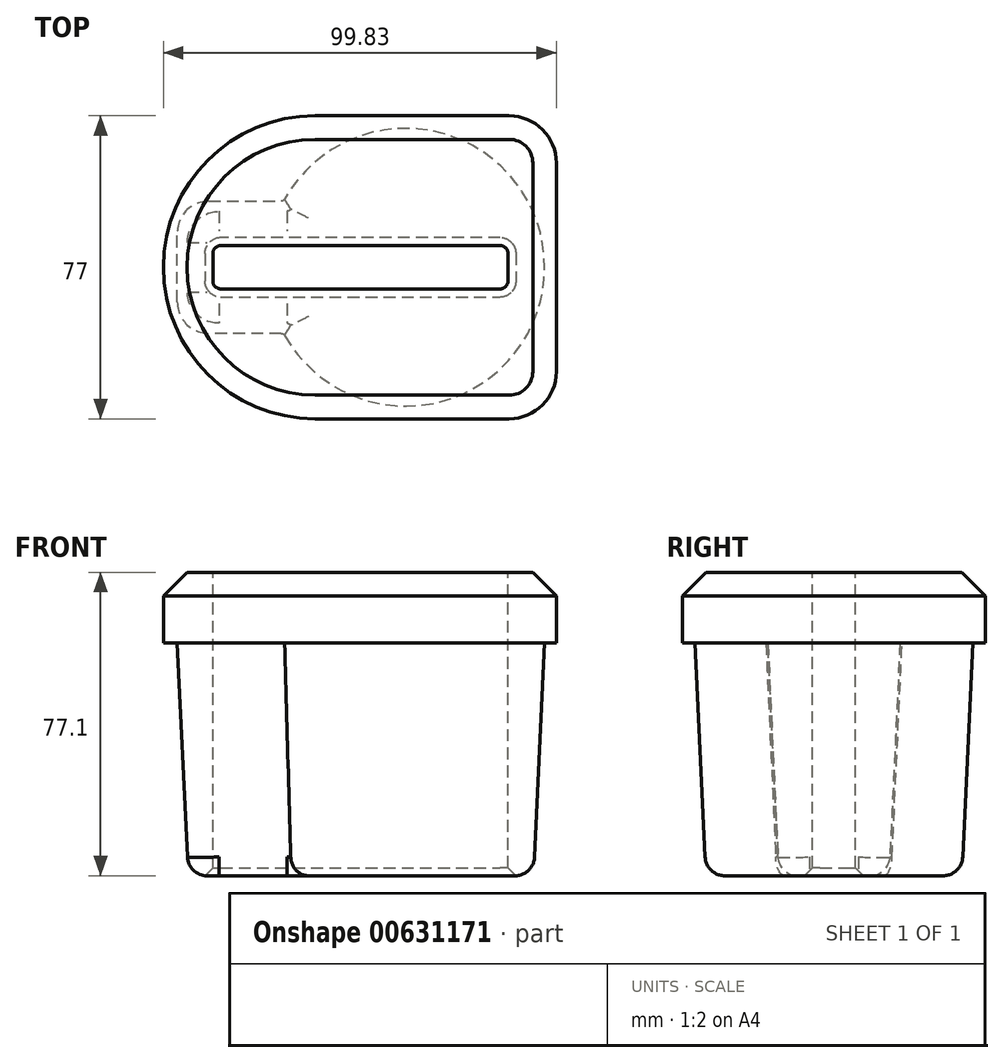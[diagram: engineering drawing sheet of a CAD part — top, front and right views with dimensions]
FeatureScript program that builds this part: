
annotation { "Feature Type Name" : "Feature", "Feature Type Description" : "" }
export const myFeature = defineFeature(function(context is Context, id is Id, definition is map)
    precondition{}
    {
        {
            var Q0;
            Q0=qCreatedBy(makeId("Top.planeOp"),FACE);
            var sketch = newSketch(context, id + "F0", { "sketchPlane" : qUnion([Q0])});
            skCircle(sketch, "E0", {"center": v(0, 0) * mm, "radius": 32.5 * mm});
            skLineSegment(sketch, "E1.bottom", {"start": v(-55.25, -14) * mm, "end": v(0, -14) * mm});
            skLineSegment(sketch, "E1.top", {"start": v(-55.25, 14) * mm, "end": v(0, 14) * mm});
            skLineSegment(sketch, "E1.left", {"start": v(-55.25, -14) * mm, "end": v(-55.25, 14) * mm});
            skLineSegment(sketch, "E1.right", {"start": v(0, -14) * mm, "end": v(0, 14) * mm});
            skSolve(sketch);
        }
        {
            var Q0;
            {var subQ5=sQuery(id+"F0.wireOp",EDGE,"E1.right");Q0=makeQuery(id+"F0.imprint","IMPRINT",FACE,{"disambiguationData":[TD([[makeQuery(id+"F0.imprint","IMPRINT",EDGE,{"derivedFrom":subQ5}),-1.0]])]});}
            var Q1;
            {var subQ5=sQuery(id+"F0.wireOp",EDGE,"E1.right");Q1=makeQuery(id+"F0.imprint","IMPRINT",FACE,{"disambiguationData":[TD([[makeQuery(id+"F0.imprint","IMPRINT",EDGE,{"derivedFrom":subQ5}),1.0]])]});}
            extrude(context, id + "F1", {"entities" : qUnion([Q0, Q1]), "depth" : 59.1 * mm, "offsetDistance" : 25 * mm, "hasDraft" : true, "draftAngle" : 2.7 * degree});
        }
        {
            var Q0;
            {var subQ5=sQuery(id+"F0.wireOp",EDGE,"E1.left");Q0=makeQuery(id+"F0.imprint","IMPRINT",FACE,{"disambiguationData":[TD([[makeQuery(id+"F0.imprint","IMPRINT",EDGE,{"derivedFrom":subQ5}),-1.0]])]});}
            extrude(context, id + "F2", {"entities" : qUnion([Q0]), "operationType" : NewBodyOperationType.ADD, "depth" : 59.1 * mm, "offsetDistance" : 25 * mm, "hasDraft" : true, "draftAngle" : 2.7 * degree});
        }
        {
            var Q0;
            {var subQ0=sQuery(id+"F0.wireOp",EDGE,"E0");Q0=makeQuery(id+"F2.boolean.opBoolean","MERGE",FACE,{"derivedFrom":[makeQuery(id+"F1.opExtrude","CAP_FACE",FACE,{"disambiguationData":[OSD([subQ0])],"isStart":false}),makeQuery(id+"F2.opExtrude","CAP_FACE",FACE,{"disambiguationData":[OSD([subQ0,sQuery(id+"F0.wireOp",EDGE,"E1.bottom"),sQuery(id+"F0.wireOp",EDGE,"E1.top"),sQuery(id+"F0.wireOp",EDGE,"E1.left")])],"isStart":false})]});}
            var sketch = newSketch(context, id + "F3", { "sketchPlane" : qUnion([Q0])});
            skArc(sketch, "E2", {"start": v(-23.04, 38.5) * mm, "mid": v(-61.54, 0) * mm, "end": v(-23.04, -38.5) * mm});
            skPoint(sketch, "E2.centerSnap0", {"position": v(-58.04, 0) * mm});
            skLineSegment(sketch, "E3.bottom", {"start": v(-23.04, -38.5) * mm, "end": v(26.29, -38.5) * mm});
            skLineSegment(sketch, "E3.top", {"start": v(-23.04, 38.5) * mm, "end": v(26.29, 38.5) * mm});
            skLineSegment(sketch, "E3.right", {"start": v(38.29, -26.5) * mm, "end": v(38.29, 26.5) * mm});
            skPoint(sketch, "E4.visualSharp", {"position": v(38.29, 38.5) * mm});
            skArc(sketch, "E4.filletArc", {"start": v(38.29, 26.5) * mm, "mid": v(34.77, 34.99) * mm, "end": v(26.29, 38.5) * mm});
            skPoint(sketch, "E5.visualSharp", {"position": v(38.29, -38.5) * mm});
            skArc(sketch, "E5.filletArc", {"start": v(26.29, -38.5) * mm, "mid": v(34.77, -34.99) * mm, "end": v(38.29, -26.5) * mm});
            skSolve(sketch);
        }
        {
            var Q0;
            Q0=makeQuery(id+"F2.opExtrude","SWEPT_EDGE",EDGE,{"disambiguationData":[OSD([sQuery(id+"F0.wireOp",EDGE,"E1.top"),sQuery(id+"F0.wireOp",EDGE,"E1.left")])]});
            var Q1;
            Q1=makeQuery(id+"F2.opExtrude","SWEPT_EDGE",EDGE,{"disambiguationData":[OSD([sQuery(id+"F0.wireOp",EDGE,"E1.bottom"),sQuery(id+"F0.wireOp",EDGE,"E1.left")])]});
            fillet(context, id + "F4", {"entities" : qUnion([Q0, Q1]), "radius" : 8 * mm, "tangentPropagation" : true, "allowEdgeOverflow" : false});
        }
        {
            var Q0;
            Q0=makeQuery(id+"F2.boolean.opBoolean","INTERSECT",EDGE,{"derivedFrom":[makeQuery(id+"F1.opExtrude","SWEPT_FACE",FACE,{"disambiguationData":[OSD([sQuery(id+"F0.wireOp",EDGE,"E0")])]}),makeQuery(id+"F2.opExtrude","SWEPT_FACE",FACE,{"disambiguationData":[OSD([sQuery(id+"F0.wireOp",EDGE,"E1.bottom")])]})]});
            var Q1;
            Q1=makeQuery(id+"F2.boolean.opBoolean","INTERSECT",EDGE,{"derivedFrom":[makeQuery(id+"F1.opExtrude","SWEPT_FACE",FACE,{"disambiguationData":[OSD([sQuery(id+"F0.wireOp",EDGE,"E0")])]}),makeQuery(id+"F2.opExtrude","SWEPT_FACE",FACE,{"disambiguationData":[OSD([sQuery(id+"F0.wireOp",EDGE,"E1.top")])]})]});
            fillet(context, id + "F5", {"entities" : qUnion([Q0, Q1]), "radius" : 1 * mm, "tangentPropagation" : true, "allowEdgeOverflow" : false});
        }
        {
            var Q0;
            {var subQ5=sQuery(id+"F3.wireOp",EDGE,"E3.bottom");Q0=makeQuery(id+"F3.imprint","IMPRINT",FACE,{"disambiguationData":[TD([[makeQuery(id+"F3.imprint","IMPRINT",EDGE,{"derivedFrom":subQ5}),1.0]])]});}
            var Q1;
            {var subQ0=sQuery(id+"F3.wireOp",EDGE,"E2");var subQ1=makeQuery(id+"F2.opExtrude","CAP_EDGE",EDGE,{"disambiguationData":[OSD([sQuery(id+"F0.wireOp",EDGE,"E1.left")])],"isStart":false});var subQ2=makeQuery(id+"F3.imprint","INTERSECT",VERTEX,{"disambiguationData":[OD(0.0)],"derivedFrom":[subQ1,subQ0]});Q1=makeQuery(id+"F3.imprint","IMPRINT",FACE,{"disambiguationData":[TD([[makeQuery(id+"F3.imprint","IMPRINT",EDGE,{"disambiguationData":[TD([[subQ2,-1.0]])],"derivedFrom":subQ0}),1.0]])]});}
            var Q2;
            {var subQ0=makeQuery(id+"F1.opExtrude","CAP_EDGE",EDGE,{"disambiguationData":[OSD([sQuery(id+"F0.wireOp",EDGE,"E0")])],"isStart":false});Q2=makeQuery(id+"F3.imprint","IMPRINT",FACE,{"disambiguationData":[TD([[makeQuery(id+"F3.imprint","IMPRINT",EDGE,{"derivedFrom":subQ0}),1.0]])]});}
            extrude(context, id + "F6", {"entities" : qUnion([Q0, Q1, Q2]), "operationType" : NewBodyOperationType.ADD, "depth" : 18 * mm, "offsetDistance" : 25 * mm});
        }
        {
            var Q0;
            Q0=makeQuery(id+"F6.opExtrude","CAP_FACE",FACE,{"disambiguationData":[OSD([sQuery(id+"F3.wireOp",EDGE,"E2"),sQuery(id+"F3.wireOp",EDGE,"E3.bottom"),sQuery(id+"F3.wireOp",EDGE,"E3.top"),sQuery(id+"F3.wireOp",EDGE,"E3.right"),sQuery(id+"F3.wireOp",EDGE,"E4.filletArc"),sQuery(id+"F3.wireOp",EDGE,"E5.filletArc")])],"isStart":false});
            var sketch = newSketch(context, id + "F7", { "sketchPlane" : qUnion([Q0])});
            skLineSegment(sketch, "E6.right", {"start": v(0, -5.5) * mm, "end": v(0, 5.5) * mm});
            skLineSegment(sketch, "E7.bottom", {"start": v(-49, -5.5) * mm, "end": v(26, -5.5) * mm});
            skLineSegment(sketch, "E7.top", {"start": v(-49, 5.5) * mm, "end": v(26, 5.5) * mm});
            skLineSegment(sketch, "E7.left", {"start": v(-49, -5.5) * mm, "end": v(-49, 5.5) * mm});
            skLineSegment(sketch, "E7.right", {"start": v(26, -5.5) * mm, "end": v(26, 5.5) * mm});
            skSolve(sketch);
        }
        {
            var Q0;
            {var subQ0=sQuery(id+"F7.wireOp",EDGE,"E6.right");Q0=makeQuery(id+"F7.imprint","IMPRINT",FACE,{"disambiguationData":[TD([[makeQuery(id+"F7.imprint","IMPRINT",EDGE,{"derivedFrom":subQ0}),-1.0]])]});}
            var Q1;
            {var subQ0=sQuery(id+"F7.wireOp",EDGE,"E6.right");Q1=makeQuery(id+"F7.imprint","IMPRINT",FACE,{"disambiguationData":[TD([[makeQuery(id+"F7.imprint","IMPRINT",EDGE,{"derivedFrom":subQ0}),1.0]])]});}
            extrude(context, id + "F8", {"entities" : qUnion([Q0, Q1]), "operationType" : NewBodyOperationType.REMOVE, "oppositeDirection" : true, "depth" : 150 * mm, "offsetDistance" : 25 * mm});
        }
        {
            var Q0;
            Q0=makeQuery(id+"F8.boolean.opBoolean","COPY",EDGE,{"derivedFrom":makeQuery(id+"F8.opExtrude","SWEPT_EDGE",EDGE,{"disambiguationData":[OSD([sQuery(id+"F7.wireOp",EDGE,"E7.bottom"),sQuery(id+"F7.wireOp",EDGE,"E7.right")])]})});
            var Q1;
            Q1=makeQuery(id+"F8.boolean.opBoolean","COPY",EDGE,{"derivedFrom":makeQuery(id+"F8.opExtrude","SWEPT_EDGE",EDGE,{"disambiguationData":[OSD([sQuery(id+"F7.wireOp",EDGE,"E7.top"),sQuery(id+"F7.wireOp",EDGE,"E7.left")])]})});
            var Q2;
            Q2=makeQuery(id+"F8.boolean.opBoolean","COPY",EDGE,{"derivedFrom":makeQuery(id+"F8.opExtrude","SWEPT_EDGE",EDGE,{"disambiguationData":[OSD([sQuery(id+"F7.wireOp",EDGE,"E7.bottom"),sQuery(id+"F7.wireOp",EDGE,"E7.left")])]})});
            var Q3;
            Q3=makeQuery(id+"F8.boolean.opBoolean","COPY",EDGE,{"derivedFrom":makeQuery(id+"F8.opExtrude","SWEPT_EDGE",EDGE,{"disambiguationData":[OSD([sQuery(id+"F7.wireOp",EDGE,"E7.top"),sQuery(id+"F7.wireOp",EDGE,"E7.right")])]})});
            fillet(context, id + "F9", {"entities" : qUnion([Q0, Q1, Q2, Q3]), "radius" : 2 * mm, "tangentPropagation" : true, "allowEdgeOverflow" : false});
        }
        {
            var Q0;
            Q0=makeQuery(id+"F6.opExtrude","CAP_EDGE",EDGE,{"disambiguationData":[OSD([sQuery(id+"F3.wireOp",EDGE,"E3.top")])],"isStart":false});
            chamfer(context, id + "F10", {"entities" : qUnion([Q0]), "width" : 6 * mm, "tangentPropagation" : true});
        }
        {
            var Q0;
            Q0=makeQuery(id+"F8.boolean.opBoolean","COPY",EDGE,{"derivedFrom":makeQuery(id+"F8.opExtrude","CAP_EDGE",EDGE,{"disambiguationData":[OSD([sQuery(id+"F7.wireOp",EDGE,"E7.top")])],"isStart":true})});
            var Q1;
            {var subQ0=sQuery(id+"F0.wireOp",EDGE,"E0");Q1=makeQuery(id+"F8.boolean.opBoolean","INTERSECT",EDGE,{"derivedFrom":[makeQuery(id+"F2.boolean.opBoolean","MERGE",FACE,{"derivedFrom":[makeQuery(id+"F1.opExtrude","CAP_FACE",FACE,{"disambiguationData":[OSD([subQ0])],"isStart":true}),makeQuery(id+"F2.opExtrude","CAP_FACE",FACE,{"disambiguationData":[OSD([subQ0,sQuery(id+"F0.wireOp",EDGE,"E1.bottom"),sQuery(id+"F0.wireOp",EDGE,"E1.top"),sQuery(id+"F0.wireOp",EDGE,"E1.left")])],"isStart":true})]}),makeQuery(id+"F8.opExtrude","SWEPT_FACE",FACE,{"disambiguationData":[OSD([sQuery(id+"F7.wireOp",EDGE,"E7.top")])]})]});}
            chamfer(context, id + "F11", {"entities" : qUnion([Q0, Q1]), "width" : 2 * mm, "tangentPropagation" : true});
        }
        {
            var Q0;
            Q0=makeQuery(id+"F2.opExtrude","CAP_EDGE",EDGE,{"disambiguationData":[OSD([sQuery(id+"F0.wireOp",EDGE,"E1.bottom")])],"isStart":true});
            fillet(context, id + "F12", {"entities" : qUnion([Q0]), "radius" : 5 * mm, "tangentPropagation" : true, "allowEdgeOverflow" : false});
        }
    });
